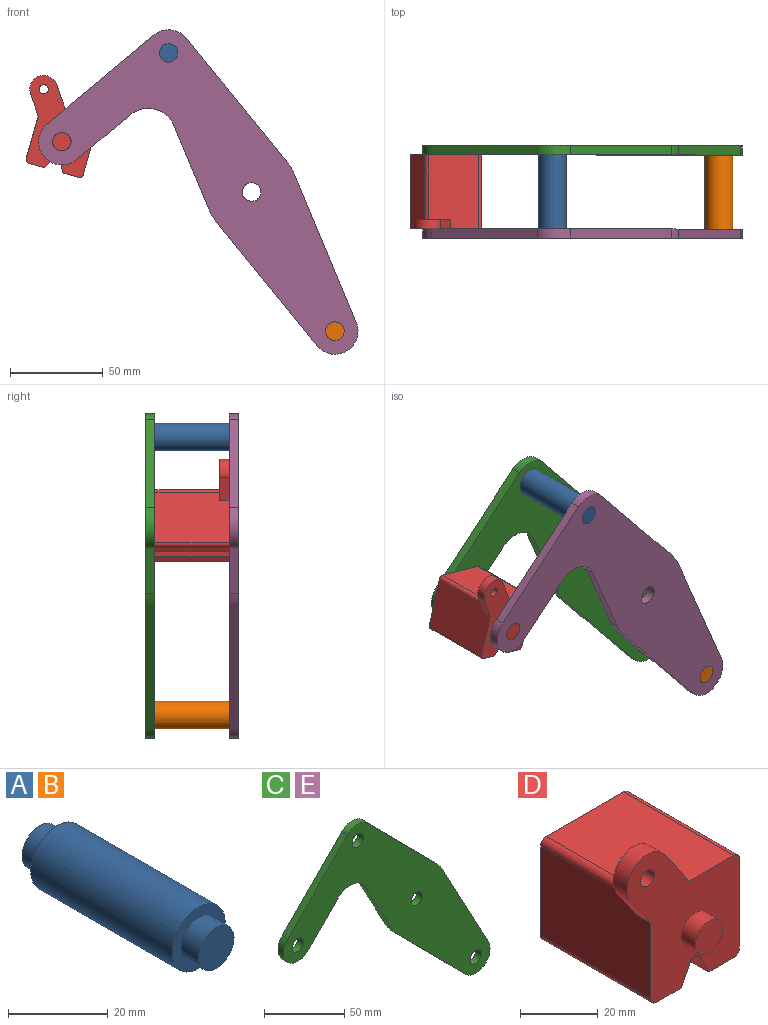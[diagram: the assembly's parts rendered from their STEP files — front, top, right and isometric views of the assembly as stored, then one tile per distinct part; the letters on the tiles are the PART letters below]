
ASSEMBLY  parts=5 mates=3
PART A: 7 faces, bbox 15x50x15 mm
  f0: cylinder r=7.5mm len=40mm, axis (0,-1,0), area 1885mm2, adj f2,f5
  f1: cylinder r=5mm len=10mm, axis (0,1,0), area 157.1mm2, adj f2,f3
  f2: plane 15x15mm, normal (0,-1,0), area 98.2mm2, adj f0,f1
  f3: plane 10x10mm, normal (0,-1,0), area 78.5mm2, adj f1
  f4: cylinder r=5mm len=10mm, axis (0,-1,0), area 157.1mm2, adj f5,f6
  f5: plane 15x15mm, normal (0,1,0), area 98.2mm2, adj f0,f4
  f6: plane 10x10mm, normal (0,1,0), area 78.5mm2, adj f4
PART B: same geometry as A
PART C: 18 faces, bbox 181.7x5x165.8 mm
  f0: plane 43.49x23.35mm, normal (-0.88,0,-0.47), area 246.8mm2, adj f1,f14,f16,f17
  f1: cylinder r=25mm len=5.75mm, axis (0,1,0), area 35.8mm2, adj f0,f2,f16,f17
  f2: plane 61.6x60.87mm, normal (-0.71,0,-0.7), area 433mm2, adj f1,f3,f16,f17
  f3: cylinder r=12.5mm len=21.39mm, axis (0,1,0), area 178.4mm2, adj f2,f4,f16,f17
  f4: plane 76.3x40.96mm, normal (0.88,0,0.47), area 433mm2, adj f3,f5,f16,f17
  f5: cylinder r=25mm len=5.75mm, axis (0,1,0), area 35.8mm2, adj f4,f6,f16,f17
  f6: plane 61.6x60.87mm, normal (0.71,0,0.7), area 433mm2, adj f5,f7,f16,f17
  f7: cylinder r=12.5mm len=17.78mm, axis (0,1,0), area 98.9mm2, adj f6,f8,f16,f17
  f8: plane 53.35x52.71mm, normal (-0.71,0,0.7), area 375mm2, adj f7,f9,f16,f17
  f9: cylinder r=12.5mm len=21.39mm, axis (0,1,0), area 196.3mm2, adj f8,f10,f16,f17
  f10: plane 26.86x26.54mm, normal (0.71,0,-0.7), area 188.8mm2, adj f9,f14,f16,f17
  f11: cylinder r=5mm len=10mm, axis (0,1,0), area 157.1mm2, adj f16,f17
  f12: cylinder r=5mm len=10mm, axis (0,1,0), area 157.1mm2, adj f16,f17
  f13: cylinder r=5mm len=10mm, axis (0,1,0), area 157.1mm2, adj f16,f17
  f14: cylinder r=15mm len=23.89mm, axis (0,1,0), area 140.2mm2, adj f0,f10,f16,f17
  f15: cylinder r=5mm len=10mm, axis (0,1,0), area 157.1mm2, adj f16,f17
  f16: plane 181.66x165.78mm, normal (0,-1,0), area 8710.1mm2, adj f0,f1,f2,f3,f4,f5,f6,f7
  f17: plane 181.66x165.78mm, normal (0,1,0), area 8710.1mm2, adj f0,f1,f2,f3,f4,f5,f6,f7
PART D: 23 faces, bbox 40.8x50x48.1 mm
  f0: plane 40x28.08mm, normal (-1,0,0), area 1101.9mm2, adj f7,f10,f14,f15,f19,f22
  f1: plane 40x6.42mm, normal (-0.89,0,-0.45), area 287.2mm2, adj f6,f7,f10,f13
  f2: plane 40x6.42mm, normal (0.89,0,-0.45), area 287.2mm2, adj f3,f7,f10,f13
  f3: plane 40x9.04mm, normal (0,0,-1), area 361.6mm2, adj f2,f7,f10,f14
  f4: plane 40x28.08mm, normal (0,0,1), area 1063.4mm2, adj f7,f10,f15,f16,f18,f22
  f5: plane 40x28.08mm, normal (1,0,0), area 1123.1mm2, adj f7,f10,f16,f17
  f6: plane 40x9.04mm, normal (0,0,-1), area 361.6mm2, adj f1,f7,f10,f17
  f7: plane 48.1x40.77mm, normal (0,-1,0), area 1139.9mm2, adj f0,f1,f2,f3,f4,f5,f6,f9
  f8: plane 10x10mm, normal (0,-1,0), area 78.5mm2, adj f9
  f9: cylinder r=5mm len=10mm, axis (0,1,0), area 157.1mm2, adj f7,f8
  f10: plane 32.08x32.08mm, normal (0,1,0), area 900.6mm2, adj f0,f1,f2,f3,f4,f5,f6,f12
  f11: plane 10x10mm, normal (0,1,0), area 78.5mm2, adj f12
  f12: cylinder r=5mm len=10mm, axis (0,-1,0), area 157.1mm2, adj f10,f11
  f13: cylinder r=2mm len=40mm, axis (0,1,0), area 177.1mm2, adj f1,f2,f7,f10
  f14: cylinder r=2mm len=40mm, axis (0,1,0), area 125.7mm2, adj f0,f3,f7,f10
  f15: cylinder r=2mm len=35mm, axis (0,-1,0), area 110mm2, adj f0,f4,f10,f22
  f16: cylinder r=2mm len=40mm, axis (0,1,0), area 125.7mm2, adj f4,f5,f7,f10
  f17: cylinder r=2mm len=40mm, axis (0,-1,0), area 125.7mm2, adj f5,f6,f7,f10
  f18: plane 12.83x9mm, normal (0.82,0,0.57), area 78.3mm2, adj f4,f7,f21,f22
  f19: plane 10.45x7.33mm, normal (-0.82,0,-0.57), area 63.8mm2, adj f0,f7,f21,f22
  f20: cylinder r=2.5mm len=5mm, axis (0,-1,0), area 78.5mm2, adj f7,f22
  f21: cylinder r=7.5mm len=13.64mm, axis (0,-1,0), area 117.8mm2, adj f7,f18,f19,f22
  f22: plane 22.64x22.26mm, normal (0,1,0), area 239.3mm2, adj f0,f4,f15,f18,f19,f20,f21
PART E: same geometry as C
PLACE A rot(axis=(0,1,0),5.6deg) t=(0,-20,0)mm
PLACE B rot(axis=(0,1,0),5.6deg) t=(89.77,-20,-150.22)mm
PLACE C rot(axis=(0,1,0),5.6deg) t=(0,25,0)mm
PLACE D rot(axis=(0,1,0),15.9deg) t=(-6.54,-20,-17.98)mm
PLACE E rot(axis=(0,1,0),5.6deg) t=(0,-20,0)mm fixed
MATE revolute D.f9 <-> E.f9  axis (0,-1,0) through (-102.54,-20,27.14)mm
MATE fastened E.f3 <-> B.f0  axis (0,1,0) through (44.88,-20,-75.11)mm
MATE fastened C.f7 <-> A.f0  axis (0,-1,0) through (-44.88,20,75.11)mm
